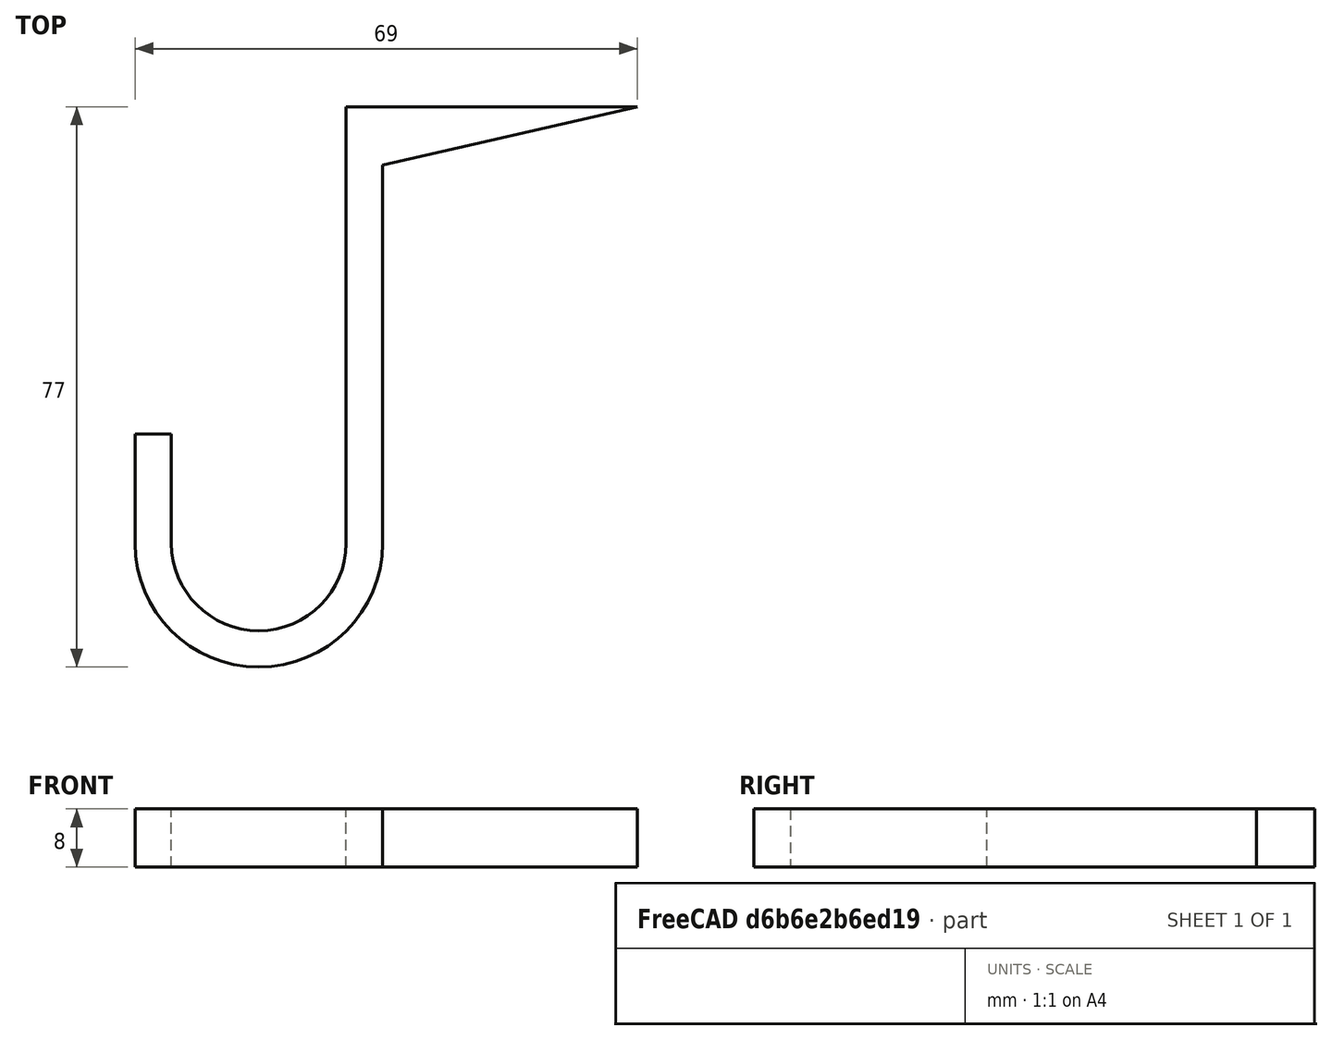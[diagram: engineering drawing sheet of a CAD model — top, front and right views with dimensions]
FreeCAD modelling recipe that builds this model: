
FCSTD DOCUMENT  (FreeCAD 0.14R3702 (Git))
Label: cunya_percha
License: CC-BY 3.0
LicenseURL: http://creativecommons.org/licenses/by/3.0/
objects: Sketcher::SketchObject×1, PartDesign::Pad×1
note: 3 computed .brp shape members not serialized (recipe doc carries the construction recipe); baked Part::Feature solids carry a one-line shape summary decoded from their .brp

FEATURE [Sketcher::SketchObject] Sketch
  sketch-geometry (9):
    g0: LineSegment StartX=-2.5 StartY=30 StartZ=0 EndX=37.5 EndY=30 EndZ=0
    g1: LineSegment StartX=37.5 StartY=30 StartZ=0 EndX=2.5 EndY=22 EndZ=0
    g2: LineSegment StartX=2.5 StartY=22 StartZ=0 EndX=2.5 EndY=-30 EndZ=0
    g3: LineSegment StartX=-2.5 StartY=-30 StartZ=0 EndX=-2.5 EndY=30 EndZ=0
    g4: ArcOfCircle CenterX=-14.5 CenterY=-30 CenterZ=0 NormalX=0 NormalY=0 NormalZ=1 Radius=12 StartAngle=3.14159 EndAngle=6.28319
    g5: ArcOfCircle CenterX=-14.5 CenterY=-30 CenterZ=0 NormalX=0 NormalY=0 NormalZ=1 Radius=17 StartAngle=3.14159 EndAngle=6.28319
    g6: LineSegment StartX=-31.5 StartY=-30 StartZ=0 EndX=-31.5 EndY=-15 EndZ=0
    g7: LineSegment StartX=-31.5 StartY=-15 StartZ=0 EndX=-26.5 EndY=-15 EndZ=0
    g8: LineSegment StartX=-26.5 StartY=-15 StartZ=0 EndX=-26.5 EndY=-30 EndZ=0
  constraints (26):
    c: Horizontal(g0)
    c: Coincident(g0,g1)
    c: Coincident(g1,g2)
    c: Vertical(g2)
    c: Coincident(g3,g0)
    c: Vertical(g3)
    c: Coincident(g4,g3)
    c: Coincident(g5,g4)
    c: Coincident(g5,g2)
    c: Tangent(g5,g6)
    c: Coincident(g6,g7)
    c: Horizontal(g7)
    c: Coincident(g7,g8)
    c: Coincident(g8,g4)
    c: Vertical(g8)
    c: Vertical(g6)
    c: Tangent(g2,g5)
    c: Radius(g4) = 12
    c: DistanceX(g7) = 5
    c: Distance(g1,g0) = 8
    c: DistanceX(g0) = 40
    c: DistanceY(g8) = -15
    c: Symmetric(g2,g3,g-2)
    c: Symmetric(g0,g3,g-1)
    c: DistanceY(g3) = 60
    c: Tangent(g8,g4)
FEATURE [PartDesign::Pad] Pad
  Length = 8
  Length2 = 100
  Sketch = -> Sketch
  Type = 0
